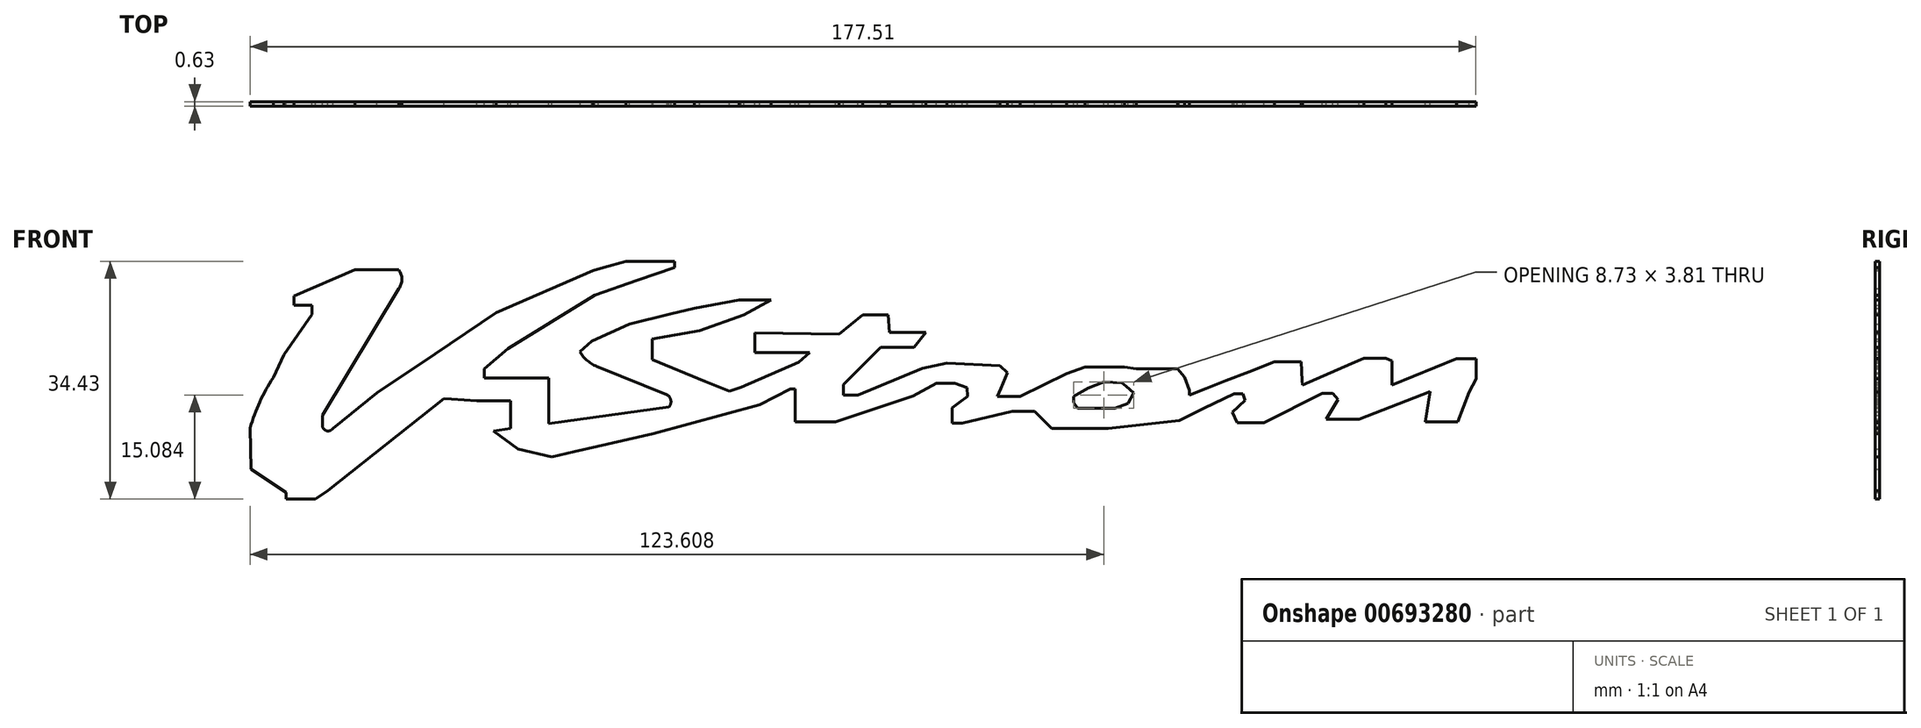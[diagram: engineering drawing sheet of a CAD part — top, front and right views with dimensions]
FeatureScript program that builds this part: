
annotation { "Feature Type Name" : "Feature", "Feature Type Description" : "" }
export const myFeature = defineFeature(function(context is Context, id is Id, definition is map)
    precondition{}
    {
        {
            var Q0;
            Q0=qCreatedBy(makeId("Front.planeOp"),FACE);
            var sketch = newSketch(context, id + "F0", { "sketchPlane" : qUnion([Q0])});
            skLineSegment(sketch, "E0", {"start": v(61.18, 22.23) * mm, "end": v(67.3, 23.37) * mm});
            skLineSegment(sketch, "E1", {"start": v(67.3, 23.37) * mm, "end": v(70.1, 23.37) * mm});
            skLineSegment(sketch, "E2", {"start": v(70.1, 23.37) * mm, "end": v(71.75, 23.37) * mm});
            skLineSegment(sketch, "E3", {"start": v(71.75, 23.37) * mm, "end": v(68, 21.28) * mm});
            skLineSegment(sketch, "E4", {"start": v(68, 21.28) * mm, "end": v(61.86, 19.14) * mm});
            skLineSegment(sketch, "E5", {"start": v(61.86, 19.14) * mm, "end": v(55.32, 17.94) * mm});
            skLineSegment(sketch, "E6", {"start": v(55.32, 17.94) * mm, "end": v(55.32, 15.1) * mm});
            skLineSegment(sketch, "E7", {"start": v(55.32, 15.1) * mm, "end": v(62.67, 12.12) * mm});
            skLineSegment(sketch, "E8", {"start": v(62.67, 12.12) * mm, "end": v(66, 10.76) * mm});
            skLineSegment(sketch, "E9", {"start": v(66, 10.76) * mm, "end": v(67.6, 11.32) * mm});
            skLineSegment(sketch, "E10", {"start": v(67.6, 11.32) * mm, "end": v(75.53, 14.78) * mm});
            skLineSegment(sketch, "E11", {"start": v(75.53, 14.78) * mm, "end": v(77.05, 16.07) * mm});
            skLineSegment(sketch, "E12", {"start": v(77.05, 16.07) * mm, "end": v(69.52, 16.07) * mm});
            skLineSegment(sketch, "E13", {"start": v(69.52, 16.07) * mm, "end": v(69.52, 18.83) * mm});
            skLineSegment(sketch, "E14", {"start": v(69.52, 18.83) * mm, "end": v(81.09, 18.6) * mm});
            skLineSegment(sketch, "E15", {"start": v(81.09, 18.6) * mm, "end": v(84.4, 21.29) * mm});
            skLineSegment(sketch, "E16", {"start": v(84.4, 21.29) * mm, "end": v(87.87, 21.29) * mm});
            skLineSegment(sketch, "E17", {"start": v(87.87, 21.29) * mm, "end": v(88.07, 18.87) * mm});
            skLineSegment(sketch, "E18", {"start": v(88.07, 18.87) * mm, "end": v(93.1, 18.87) * mm});
            skLineSegment(sketch, "E19", {"start": v(93.1, 18.87) * mm, "end": v(91.44, 16.8) * mm});
            skLineSegment(sketch, "E20", {"start": v(91.44, 16.8) * mm, "end": v(86.88, 16.8) * mm});
            skLineSegment(sketch, "E21", {"start": v(86.88, 16.8) * mm, "end": v(81.75, 11.67) * mm});
            skLineSegment(sketch, "E22", {"start": v(81.75, 11.67) * mm, "end": v(81.75, 10.24) * mm});
            skLineSegment(sketch, "E23", {"start": v(81.75, 10.24) * mm, "end": v(83.7, 10.24) * mm});
            skLineSegment(sketch, "E24", {"start": v(83.7, 10.24) * mm, "end": v(92.6, 13.94) * mm});
            skLineSegment(sketch, "E25", {"start": v(92.6, 13.94) * mm, "end": v(95.98, 14.63) * mm});
            skLineSegment(sketch, "E26", {"start": v(95.98, 14.63) * mm, "end": v(103.29, 14.27) * mm});
            skLineSegment(sketch, "E27", {"start": v(103.29, 14.27) * mm, "end": v(104.36, 13.3) * mm});
            skLineSegment(sketch, "E28", {"start": v(104.36, 13.3) * mm, "end": v(103.4, 11.1) * mm});
            skLineSegment(sketch, "E29", {"start": v(103.4, 11.1) * mm, "end": v(102.94, 10.06) * mm});
            skLineSegment(sketch, "E30", {"start": v(102.94, 10.06) * mm, "end": v(103.99, 10.06) * mm});
            skLineSegment(sketch, "E31", {"start": v(103.99, 10.06) * mm, "end": v(106.08, 10.06) * mm});
            skLineSegment(sketch, "E32", {"start": v(106.08, 10.06) * mm, "end": v(112.49, 13.2) * mm});
            skLineSegment(sketch, "E33", {"start": v(112.49, 13.2) * mm, "end": v(115.03, 14.1) * mm});
            skLineSegment(sketch, "E34", {"start": v(115.03, 14.1) * mm, "end": v(118.01, 14.1) * mm});
            skLineSegment(sketch, "E35", {"start": v(118.01, 14.1) * mm, "end": v(120.48, 14.1) * mm});
            skLineSegment(sketch, "E36", {"start": v(120.48, 14.1) * mm, "end": v(122.09, 13.88) * mm});
            skLineSegment(sketch, "E37", {"start": v(120.12, 11.9) * mm, "end": v(117.66, 12.07) * mm});
            skLineSegment(sketch, "E38", {"start": v(117.66, 12.07) * mm, "end": v(115.44, 11.18) * mm});
            skLineSegment(sketch, "E39", {"start": v(115.44, 11.18) * mm, "end": v(113.46, 10.06) * mm});
            skLineSegment(sketch, "E40", {"start": v(113.46, 10.06) * mm, "end": v(113.46, 9.22) * mm});
            skLineSegment(sketch, "E41", {"start": v(113.46, 9.22) * mm, "end": v(114.02, 8.44) * mm});
            skLineSegment(sketch, "E42", {"start": v(114.02, 8.44) * mm, "end": v(115.03, 8.44) * mm});
            skLineSegment(sketch, "E43", {"start": v(115.03, 8.44) * mm, "end": v(117.62, 8.44) * mm});
            skLineSegment(sketch, "E44", {"start": v(117.62, 8.44) * mm, "end": v(119.13, 8.44) * mm});
            skLineSegment(sketch, "E45", {"start": v(-35.24, 14.16) * mm, "end": v(-35.24, 14.16) * mm});
            skLineSegment(sketch, "E46", {"start": v(119.13, 8.44) * mm, "end": v(120.95, 9.06) * mm});
            skLineSegment(sketch, "E47", {"start": v(120.95, 9.06) * mm, "end": v(121.77, 10.51) * mm});
            skLineSegment(sketch, "E48", {"start": v(121.77, 10.51) * mm, "end": v(120.7, 11.4) * mm});
            skLineSegment(sketch, "E49", {"start": v(120.7, 11.4) * mm, "end": v(120.12, 11.9) * mm});
            skLineSegment(sketch, "E50", {"start": v(122.09, 13.88) * mm, "end": v(127.78, 13.88) * mm});
            skLineSegment(sketch, "E51", {"start": v(127.78, 13.88) * mm, "end": v(128.8, 12.7) * mm});
            skLineSegment(sketch, "E52", {"start": v(128.8, 12.7) * mm, "end": v(129.41, 10.9) * mm});
            skLineSegment(sketch, "E53", {"start": v(129.41, 10.9) * mm, "end": v(129.41, 10.23) * mm});
            skLineSegment(sketch, "E54", {"start": v(129.41, 10.23) * mm, "end": v(131.71, 11.13) * mm});
            skLineSegment(sketch, "E55", {"start": v(131.71, 11.13) * mm, "end": v(134.48, 12.2) * mm});
            skLineSegment(sketch, "E56", {"start": v(134.48, 12.2) * mm, "end": v(137.66, 13.45) * mm});
            skLineSegment(sketch, "E57", {"start": v(137.66, 13.45) * mm, "end": v(141.15, 14.8) * mm});
            skLineSegment(sketch, "E58", {"start": v(141.15, 14.8) * mm, "end": v(144.88, 14.8) * mm});
            skLineSegment(sketch, "E59", {"start": v(144.88, 14.8) * mm, "end": v(145, 12.25) * mm});
            skLineSegment(sketch, "E60", {"start": v(145, 12.25) * mm, "end": v(145.02, 11.64) * mm});
            skLineSegment(sketch, "E61", {"start": v(145.02, 11.64) * mm, "end": v(151.78, 14.55) * mm});
            skLineSegment(sketch, "E62", {"start": v(151.78, 14.55) * mm, "end": v(153.53, 15.3) * mm});
            skLineSegment(sketch, "E63", {"start": v(153.53, 15.3) * mm, "end": v(156.55, 15.3) * mm});
            skLineSegment(sketch, "E64", {"start": v(156.55, 15.3) * mm, "end": v(157.39, 14.97) * mm});
            skLineSegment(sketch, "E65", {"start": v(157.39, 14.97) * mm, "end": v(157.39, 12.95) * mm});
            skLineSegment(sketch, "E66", {"start": v(157.39, 12.95) * mm, "end": v(157.39, 12.28) * mm});
            skLineSegment(sketch, "E67", {"start": v(157.39, 12.28) * mm, "end": v(157.39, 11.6) * mm});
            skLineSegment(sketch, "E68", {"start": v(157.39, 11.6) * mm, "end": v(166.26, 15.27) * mm});
            skLineSegment(sketch, "E69", {"start": v(166.26, 15.27) * mm, "end": v(168.95, 15.27) * mm});
            skLineSegment(sketch, "E70", {"start": v(168.95, 15.27) * mm, "end": v(168.95, 12.49) * mm});
            skLineSegment(sketch, "E71", {"start": v(168.95, 12.49) * mm, "end": v(168.03, 10.64) * mm});
            skLineSegment(sketch, "E72", {"start": v(8.4, 22.6) * mm, "end": v(8.4, 21.37) * mm});
            skLineSegment(sketch, "E73", {"start": v(8.4, 21.37) * mm, "end": v(4.54, 15.76) * mm});
            skLineSegment(sketch, "E74", {"start": v(4.54, 15.76) * mm, "end": v(3.07, 12.62) * mm});
            skLineSegment(sketch, "E75", {"start": v(9.86, 7.43) * mm, "end": v(9.86, 5.91) * mm});
            skArc(sketch, "E76", {"start": v(9.86, 6.28) * mm, "mid": v(10.32, 5.35) * mm, "end": v(11.32, 5.64) * mm});
            skLineSegment(sketch, "E77", {"start": v(11.32, 5.64) * mm, "end": v(17.38, 10.52) * mm});
            skLineSegment(sketch, "E78", {"start": v(17.38, 10.52) * mm, "end": v(25.44, 15.92) * mm});
            skLineSegment(sketch, "E79", {"start": v(25.44, 15.92) * mm, "end": v(33.85, 21.57) * mm});
            skLineSegment(sketch, "E80", {"start": v(33.85, 21.57) * mm, "end": v(47.2, 27.4) * mm});
            skLineSegment(sketch, "E81", {"start": v(47.2, 27.4) * mm, "end": v(48.62, 27.8) * mm});
            skLineSegment(sketch, "E82", {"start": v(48.62, 27.8) * mm, "end": v(51.72, 28.68) * mm});
            skLineSegment(sketch, "E83", {"start": v(51.72, 28.68) * mm, "end": v(58.4, 28.68) * mm});
            skLineSegment(sketch, "E84", {"start": v(58.4, 28.68) * mm, "end": v(58.4, 27.8) * mm});
            skLineSegment(sketch, "E85", {"start": v(58.4, 27.8) * mm, "end": v(53.3, 26.05) * mm});
            skLineSegment(sketch, "E86", {"start": v(53.3, 26.05) * mm, "end": v(47.42, 24.02) * mm});
            skLineSegment(sketch, "E87", {"start": v(47.42, 24.02) * mm, "end": v(35.42, 16.61) * mm});
            skLineSegment(sketch, "E88", {"start": v(35.42, 16.61) * mm, "end": v(32.2, 13.86) * mm});
            skLineSegment(sketch, "E89", {"start": v(32.2, 13.86) * mm, "end": v(32.2, 12.57) * mm});
            skLineSegment(sketch, "E90", {"start": v(32.2, 12.57) * mm, "end": v(41.05, 12.57) * mm});
            skLineSegment(sketch, "E91", {"start": v(33.43, 5.28) * mm, "end": v(35.83, 5.6) * mm});
            skLineSegment(sketch, "E92", {"start": v(4.85, -4.12) * mm, "end": v(8.9, -4.11) * mm});
            skLineSegment(sketch, "E93", {"start": v(0, 0) * mm, "end": v(4.85, -3.21) * mm});
            skLineSegment(sketch, "E94", {"start": v(4.85, -3.21) * mm, "end": v(4.85, -4.12) * mm});
            skLineSegment(sketch, "E95", {"start": v(5.96, 22.6) * mm, "end": v(5.96, 23.91) * mm});
            skLineSegment(sketch, "E96", {"start": v(5.96, 23.91) * mm, "end": v(14.33, 27.5) * mm});
            skLineSegment(sketch, "E97", {"start": v(14.33, 27.5) * mm, "end": v(20.37, 27.5) * mm});
            skLineSegment(sketch, "E98", {"start": v(20.4, 24.92) * mm, "end": v(9.86, 7.43) * mm});
            skLineSegment(sketch, "E99", {"start": v(5.96, 22.6) * mm, "end": v(8.4, 22.6) * mm});
            skArc(sketch, "E100", {"start": v(20.4, 24.92) * mm, "mid": v(20.82, 26.21) * mm, "end": v(20.37, 27.5) * mm});
            skLineSegment(sketch, "E101", {"start": v(57.34, 10.31) * mm, "end": v(47.91, 14.1) * mm});
            skLineSegment(sketch, "E102", {"start": v(45.36, 16.2) * mm, "end": v(47, 17.65) * mm});
            skLineSegment(sketch, "E103", {"start": v(47, 17.65) * mm, "end": v(52.22, 20.04) * mm});
            skLineSegment(sketch, "E104", {"start": v(52.22, 20.04) * mm, "end": v(57.84, 21.41) * mm});
            skLineSegment(sketch, "E105", {"start": v(57.84, 21.41) * mm, "end": v(61.18, 22.23) * mm});
            skArc(sketch, "E106", {"start": v(45.36, 16.2) * mm, "mid": v(46.45, 14.92) * mm, "end": v(47.91, 14.1) * mm});
            skArc(sketch, "E107", {"start": v(57.64, 8.58) * mm, "mid": v(57.89, 9.64) * mm, "end": v(57.12, 10.4) * mm});
            skLineSegment(sketch, "E108", {"start": v(166.46, 6.55) * mm, "end": v(161.99, 6.55) * mm});
            skLineSegment(sketch, "E109", {"start": v(161.99, 6.55) * mm, "end": v(162.63, 10.72) * mm});
            skLineSegment(sketch, "E110", {"start": v(162.63, 10.72) * mm, "end": v(152.81, 6.9) * mm});
            skLineSegment(sketch, "E111", {"start": v(152.81, 6.9) * mm, "end": v(148.28, 6.9) * mm});
            skLineSegment(sketch, "E112", {"start": v(148.28, 6.9) * mm, "end": v(149.93, 9.6) * mm});
            skLineSegment(sketch, "E113", {"start": v(149.93, 9.6) * mm, "end": v(149.22, 10.48) * mm});
            skLineSegment(sketch, "E114", {"start": v(149.22, 10.48) * mm, "end": v(147.75, 10.48) * mm});
            skLineSegment(sketch, "E115", {"start": v(147.75, 10.48) * mm, "end": v(139.7, 6.43) * mm});
            skLineSegment(sketch, "E116", {"start": v(139.7, 6.43) * mm, "end": v(136.05, 6.43) * mm});
            skLineSegment(sketch, "E117", {"start": v(136.05, 6.43) * mm, "end": v(135.34, 7.9) * mm});
            skLineSegment(sketch, "E118", {"start": v(135.34, 7.9) * mm, "end": v(137.1, 9.49) * mm});
            skLineSegment(sketch, "E119", {"start": v(137.1, 9.49) * mm, "end": v(136.82, 10.43) * mm});
            skLineSegment(sketch, "E120", {"start": v(136.82, 10.43) * mm, "end": v(135.61, 10.43) * mm});
            skLineSegment(sketch, "E121", {"start": v(135.61, 10.43) * mm, "end": v(131.41, 8.4) * mm});
            skLineSegment(sketch, "E122", {"start": v(131.41, 8.4) * mm, "end": v(129.95, 7.68) * mm});
            skLineSegment(sketch, "E123", {"start": v(129.95, 7.68) * mm, "end": v(128.02, 6.75) * mm});
            skLineSegment(sketch, "E124", {"start": v(128.02, 6.75) * mm, "end": v(121.39, 6) * mm});
            skLineSegment(sketch, "E125", {"start": v(121.39, 6) * mm, "end": v(118.26, 5.64) * mm});
            skLineSegment(sketch, "E126", {"start": v(118.26, 5.64) * mm, "end": v(112.75, 5.64) * mm});
            skLineSegment(sketch, "E127", {"start": v(112.75, 5.64) * mm, "end": v(110.45, 5.64) * mm});
            skLineSegment(sketch, "E128", {"start": v(110.45, 5.64) * mm, "end": v(108.8, 7.27) * mm});
            skLineSegment(sketch, "E129", {"start": v(108.8, 7.27) * mm, "end": v(108.1, 7.96) * mm});
            skLineSegment(sketch, "E130", {"start": v(108.1, 7.96) * mm, "end": v(107.3, 7.96) * mm});
            skLineSegment(sketch, "E131", {"start": v(107.3, 7.96) * mm, "end": v(105.01, 7.96) * mm});
            skLineSegment(sketch, "E132", {"start": v(105.01, 7.96) * mm, "end": v(98.13, 6.37) * mm});
            skLineSegment(sketch, "E133", {"start": v(98.13, 6.37) * mm, "end": v(96.74, 6.37) * mm});
            skLineSegment(sketch, "E134", {"start": v(96.74, 6.37) * mm, "end": v(96.74, 8.45) * mm});
            skLineSegment(sketch, "E135", {"start": v(96.74, 8.45) * mm, "end": v(97.7, 9.2) * mm});
            skLineSegment(sketch, "E136", {"start": v(97.7, 9.2) * mm, "end": v(98.82, 10.04) * mm});
            skLineSegment(sketch, "E137", {"start": v(98.82, 10.04) * mm, "end": v(98.77, 11.27) * mm});
            skLineSegment(sketch, "E138", {"start": v(98.77, 11.27) * mm, "end": v(97.06, 11.86) * mm});
            skLineSegment(sketch, "E139", {"start": v(97.06, 11.86) * mm, "end": v(94.56, 11.86) * mm});
            skLineSegment(sketch, "E140", {"start": v(94.56, 11.86) * mm, "end": v(91.36, 10.1) * mm});
            skLineSegment(sketch, "E141", {"start": v(91.36, 10.1) * mm, "end": v(80.65, 6.52) * mm});
            skLineSegment(sketch, "E142", {"start": v(80.65, 6.52) * mm, "end": v(77.45, 6.52) * mm});
            skLineSegment(sketch, "E143", {"start": v(77.45, 6.52) * mm, "end": v(75.05, 6.52) * mm});
            skLineSegment(sketch, "E144", {"start": v(75.05, 6.52) * mm, "end": v(75.05, 11.05) * mm});
            skLineSegment(sketch, "E145", {"start": v(75.05, 11.05) * mm, "end": v(74.4, 11.05) * mm});
            skLineSegment(sketch, "E146", {"start": v(74.4, 11.05) * mm, "end": v(70.14, 8.92) * mm});
            skLineSegment(sketch, "E147", {"start": v(70.14, 8.92) * mm, "end": v(55.44, 4.9) * mm});
            skLineSegment(sketch, "E148", {"start": v(55.44, 4.9) * mm, "end": v(47.76, 3.13) * mm});
            skLineSegment(sketch, "E149", {"start": v(47.76, 3.13) * mm, "end": v(44.61, 2.4) * mm});
            skLineSegment(sketch, "E150", {"start": v(44.61, 2.4) * mm, "end": v(41.52, 1.69) * mm});
            skLineSegment(sketch, "E151", {"start": v(41.52, 1.69) * mm, "end": v(36.86, 2.77) * mm});
            skLineSegment(sketch, "E152", {"start": v(36.86, 2.77) * mm, "end": v(33.43, 5.28) * mm});
            skLineSegment(sketch, "E153", {"start": v(-0.1, 5.7) * mm, "end": v(0, 0) * mm});
            skLineSegment(sketch, "E154", {"start": v(35.83, 9.43) * mm, "end": v(35.83, 5.6) * mm});
            skLineSegment(sketch, "E155", {"start": v(41.05, 12.57) * mm, "end": v(41.05, 6.32) * mm});
            skLineSegment(sketch, "E156", {"start": v(35.83, 9.43) * mm, "end": v(31.14, 9.43) * mm});
            skLineSegment(sketch, "E157", {"start": v(31.14, 9.43) * mm, "end": v(27.66, 9.7) * mm});
            skLineSegment(sketch, "E158", {"start": v(27.66, 9.7) * mm, "end": v(26.6, 9.77) * mm});
            skLineSegment(sketch, "E159", {"start": v(26.6, 9.77) * mm, "end": v(10.57, -2.96) * mm});
            skLineSegment(sketch, "E160", {"start": v(10.57, -2.96) * mm, "end": v(8.9, -4.11) * mm});
            skLineSegment(sketch, "E161", {"start": v(41.05, 6.32) * mm, "end": v(57.64, 8.58) * mm});
            skLineSegment(sketch, "E162", {"start": v(168.03, 10.64) * mm, "end": v(166.46, 6.55) * mm});
            skArc(sketch, "E163", {"start": v(3.07, 12.62) * mm, "mid": v(1.23, 9.28) * mm, "end": v(-0.1, 5.7) * mm});
            skSolve(sketch);
        }
        {
            var Q0;
            Q0 = qSketchRegion(id + "F0", true);
            extrude(context, id + "F1", {"entities" : qUnion([Q0]), "depth" : .6 * mm, "offsetDistance" : 25 * mm});
        }
        {
            var Q0;
            Q0=makeQuery(id+"F1.opExtrude","SWEPT_BODY",BODY,{"disambiguationData":[OSD([sQuery(id+"F0.wireOp",EDGE,"E0"),sQuery(id+"F0.wireOp",EDGE,"E1"),sQuery(id+"F0.wireOp",EDGE,"E2"),sQuery(id+"F0.wireOp",EDGE,"E3"),sQuery(id+"F0.wireOp",EDGE,"E4"),sQuery(id+"F0.wireOp",EDGE,"E5"),sQuery(id+"F0.wireOp",EDGE,"E6"),sQuery(id+"F0.wireOp",EDGE,"E7"),sQuery(id+"F0.wireOp",EDGE,"E8"),sQuery(id+"F0.wireOp",EDGE,"E9"),sQuery(id+"F0.wireOp",EDGE,"E10"),sQuery(id+"F0.wireOp",EDGE,"E11"),sQuery(id+"F0.wireOp",EDGE,"E12"),sQuery(id+"F0.wireOp",EDGE,"E13"),sQuery(id+"F0.wireOp",EDGE,"E14"),sQuery(id+"F0.wireOp",EDGE,"E15"),sQuery(id+"F0.wireOp",EDGE,"E16"),sQuery(id+"F0.wireOp",EDGE,"E17"),sQuery(id+"F0.wireOp",EDGE,"E18"),sQuery(id+"F0.wireOp",EDGE,"E19"),sQuery(id+"F0.wireOp",EDGE,"E20"),sQuery(id+"F0.wireOp",EDGE,"E21"),sQuery(id+"F0.wireOp",EDGE,"E22"),sQuery(id+"F0.wireOp",EDGE,"E23"),sQuery(id+"F0.wireOp",EDGE,"E24"),sQuery(id+"F0.wireOp",EDGE,"E25"),sQuery(id+"F0.wireOp",EDGE,"E26"),sQuery(id+"F0.wireOp",EDGE,"E27"),sQuery(id+"F0.wireOp",EDGE,"E28"),sQuery(id+"F0.wireOp",EDGE,"E29"),sQuery(id+"F0.wireOp",EDGE,"E30"),sQuery(id+"F0.wireOp",EDGE,"E31"),sQuery(id+"F0.wireOp",EDGE,"E32"),sQuery(id+"F0.wireOp",EDGE,"E33"),sQuery(id+"F0.wireOp",EDGE,"E34"),sQuery(id+"F0.wireOp",EDGE,"E35"),sQuery(id+"F0.wireOp",EDGE,"E36"),sQuery(id+"F0.wireOp",EDGE,"E37"),sQuery(id+"F0.wireOp",EDGE,"E38"),sQuery(id+"F0.wireOp",EDGE,"E39"),sQuery(id+"F0.wireOp",EDGE,"E40"),sQuery(id+"F0.wireOp",EDGE,"E41"),sQuery(id+"F0.wireOp",EDGE,"E42"),sQuery(id+"F0.wireOp",EDGE,"E43"),sQuery(id+"F0.wireOp",EDGE,"E44"),sQuery(id+"F0.wireOp",EDGE,"E46"),sQuery(id+"F0.wireOp",EDGE,"E47"),sQuery(id+"F0.wireOp",EDGE,"E48"),sQuery(id+"F0.wireOp",EDGE,"E49"),sQuery(id+"F0.wireOp",EDGE,"E50"),sQuery(id+"F0.wireOp",EDGE,"E51"),sQuery(id+"F0.wireOp",EDGE,"E52"),sQuery(id+"F0.wireOp",EDGE,"E53"),sQuery(id+"F0.wireOp",EDGE,"E54"),sQuery(id+"F0.wireOp",EDGE,"E55"),sQuery(id+"F0.wireOp",EDGE,"E56"),sQuery(id+"F0.wireOp",EDGE,"E57"),sQuery(id+"F0.wireOp",EDGE,"E58"),sQuery(id+"F0.wireOp",EDGE,"E59"),sQuery(id+"F0.wireOp",EDGE,"E60"),sQuery(id+"F0.wireOp",EDGE,"E61"),sQuery(id+"F0.wireOp",EDGE,"E62"),sQuery(id+"F0.wireOp",EDGE,"E63"),sQuery(id+"F0.wireOp",EDGE,"E64"),sQuery(id+"F0.wireOp",EDGE,"E65"),sQuery(id+"F0.wireOp",EDGE,"E66"),sQuery(id+"F0.wireOp",EDGE,"E67"),sQuery(id+"F0.wireOp",EDGE,"E68"),sQuery(id+"F0.wireOp",EDGE,"E69"),sQuery(id+"F0.wireOp",EDGE,"E70"),sQuery(id+"F0.wireOp",EDGE,"E71"),sQuery(id+"F0.wireOp",EDGE,"E72"),sQuery(id+"F0.wireOp",EDGE,"E73"),sQuery(id+"F0.wireOp",EDGE,"E74"),sQuery(id+"F0.wireOp",EDGE,"E75"),sQuery(id+"F0.wireOp",EDGE,"E76"),sQuery(id+"F0.wireOp",EDGE,"E77"),sQuery(id+"F0.wireOp",EDGE,"E78"),sQuery(id+"F0.wireOp",EDGE,"E79"),sQuery(id+"F0.wireOp",EDGE,"E80"),sQuery(id+"F0.wireOp",EDGE,"E81"),sQuery(id+"F0.wireOp",EDGE,"E82"),sQuery(id+"F0.wireOp",EDGE,"E83"),sQuery(id+"F0.wireOp",EDGE,"E84"),sQuery(id+"F0.wireOp",EDGE,"E85"),sQuery(id+"F0.wireOp",EDGE,"E86"),sQuery(id+"F0.wireOp",EDGE,"E87"),sQuery(id+"F0.wireOp",EDGE,"E88"),sQuery(id+"F0.wireOp",EDGE,"E89"),sQuery(id+"F0.wireOp",EDGE,"E90"),sQuery(id+"F0.wireOp",EDGE,"E91"),sQuery(id+"F0.wireOp",EDGE,"E92"),sQuery(id+"F0.wireOp",EDGE,"E93"),sQuery(id+"F0.wireOp",EDGE,"E94"),sQuery(id+"F0.wireOp",EDGE,"E95"),sQuery(id+"F0.wireOp",EDGE,"E96"),sQuery(id+"F0.wireOp",EDGE,"E97"),sQuery(id+"F0.wireOp",EDGE,"E98"),sQuery(id+"F0.wireOp",EDGE,"E99"),sQuery(id+"F0.wireOp",EDGE,"E100"),sQuery(id+"F0.wireOp",EDGE,"E101"),sQuery(id+"F0.wireOp",EDGE,"E102"),sQuery(id+"F0.wireOp",EDGE,"E103"),sQuery(id+"F0.wireOp",EDGE,"E104"),sQuery(id+"F0.wireOp",EDGE,"E105"),sQuery(id+"F0.wireOp",EDGE,"E106"),sQuery(id+"F0.wireOp",EDGE,"E107"),sQuery(id+"F0.wireOp",EDGE,"E108"),sQuery(id+"F0.wireOp",EDGE,"E109"),sQuery(id+"F0.wireOp",EDGE,"E110"),sQuery(id+"F0.wireOp",EDGE,"E111"),sQuery(id+"F0.wireOp",EDGE,"E112"),sQuery(id+"F0.wireOp",EDGE,"E113"),sQuery(id+"F0.wireOp",EDGE,"E114"),sQuery(id+"F0.wireOp",EDGE,"E115"),sQuery(id+"F0.wireOp",EDGE,"E116"),sQuery(id+"F0.wireOp",EDGE,"E117"),sQuery(id+"F0.wireOp",EDGE,"E118"),sQuery(id+"F0.wireOp",EDGE,"E119"),sQuery(id+"F0.wireOp",EDGE,"E120"),sQuery(id+"F0.wireOp",EDGE,"E121"),sQuery(id+"F0.wireOp",EDGE,"E122"),sQuery(id+"F0.wireOp",EDGE,"E123"),sQuery(id+"F0.wireOp",EDGE,"E124"),sQuery(id+"F0.wireOp",EDGE,"E125"),sQuery(id+"F0.wireOp",EDGE,"E126"),sQuery(id+"F0.wireOp",EDGE,"E127"),sQuery(id+"F0.wireOp",EDGE,"E128"),sQuery(id+"F0.wireOp",EDGE,"E129"),sQuery(id+"F0.wireOp",EDGE,"E130"),sQuery(id+"F0.wireOp",EDGE,"E131"),sQuery(id+"F0.wireOp",EDGE,"E132"),sQuery(id+"F0.wireOp",EDGE,"E133"),sQuery(id+"F0.wireOp",EDGE,"E134"),sQuery(id+"F0.wireOp",EDGE,"E135"),sQuery(id+"F0.wireOp",EDGE,"E136"),sQuery(id+"F0.wireOp",EDGE,"E137"),sQuery(id+"F0.wireOp",EDGE,"E138"),sQuery(id+"F0.wireOp",EDGE,"E139"),sQuery(id+"F0.wireOp",EDGE,"E140"),sQuery(id+"F0.wireOp",EDGE,"E141"),sQuery(id+"F0.wireOp",EDGE,"E142"),sQuery(id+"F0.wireOp",EDGE,"E143"),sQuery(id+"F0.wireOp",EDGE,"E144"),sQuery(id+"F0.wireOp",EDGE,"E145"),sQuery(id+"F0.wireOp",EDGE,"E146"),sQuery(id+"F0.wireOp",EDGE,"E147"),sQuery(id+"F0.wireOp",EDGE,"E148"),sQuery(id+"F0.wireOp",EDGE,"E149"),sQuery(id+"F0.wireOp",EDGE,"E150"),sQuery(id+"F0.wireOp",EDGE,"E151"),sQuery(id+"F0.wireOp",EDGE,"E152"),sQuery(id+"F0.wireOp",EDGE,"E153"),sQuery(id+"F0.wireOp",EDGE,"E154"),sQuery(id+"F0.wireOp",EDGE,"E155"),sQuery(id+"F0.wireOp",EDGE,"E156"),sQuery(id+"F0.wireOp",EDGE,"E157"),sQuery(id+"F0.wireOp",EDGE,"E158"),sQuery(id+"F0.wireOp",EDGE,"E159"),sQuery(id+"F0.wireOp",EDGE,"E160"),sQuery(id+"F0.wireOp",EDGE,"E161"),sQuery(id+"F0.wireOp",EDGE,"E162"),sQuery(id+"F0.wireOp",EDGE,"E163")])]});
            var Q1;
            Q1=qCreatedBy(makeId("Origin.pointOp"),VERTEX);
            transform(context, id + "F2", {"entities" : qUnion([Q0]), "transformType" : TransformType.SCALE_UNIFORMLY, "scale" : 1.05, "scalePoint" : qUnion([Q1]), "makeCopy" : false});
        }
    });
